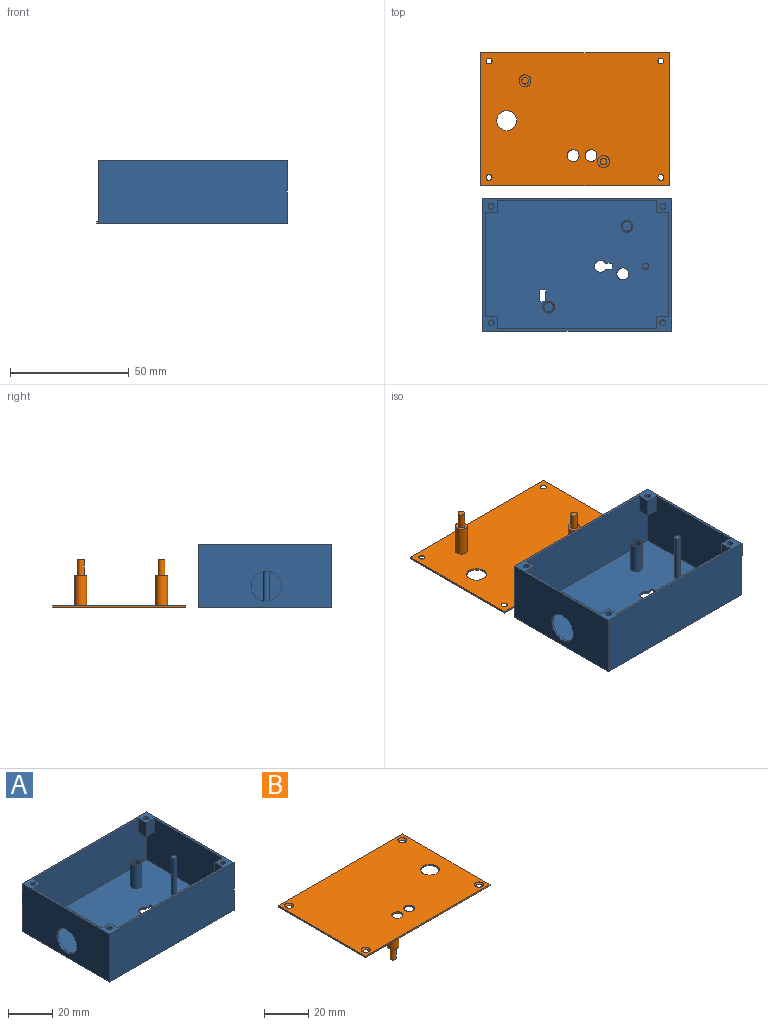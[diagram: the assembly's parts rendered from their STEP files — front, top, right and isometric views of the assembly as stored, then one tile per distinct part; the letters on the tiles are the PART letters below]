
ASSEMBLY  parts=2 mates=1
PART A: 47 faces, bbox 79.4x56x26.4 mm
  f0: plane 79.38x56.05mm, normal (0,0,-1), area 4390.6mm2, adj f6,f7,f8,f9,f10,f36,f37,f38
  f1: plane 77.38x54.05mm, normal (0,0,1), area 4079.4mm2, adj f2,f3,f4,f5,f10,f12,f16,f36
  f2: plane 54.05x25.4mm, normal (-1,0,0), area 1295.3mm2, adj f1,f3,f5,f19,f24,f27,f33,f35
  f3: plane 77.38x25.4mm, normal (0,1,0), area 1888.1mm2, adj f1,f2,f4,f19,f26,f27,f28,f31
  f4: plane 54.05x25.4mm, normal (1,0,0), area 1168.7mm2, adj f1,f3,f5,f19,f22,f23,f30,f31
  f5: plane 77.38x25.4mm, normal (0,-1,0), area 1888.1mm2, adj f1,f2,f4,f19,f20,f23,f32,f35
  f6: plane 56.05x26.4mm, normal (-1,0,0), area 1352.9mm2, adj f0,f7,f9,f19,f40
  f7: plane 79.38x26.4mm, normal (0,-1,0), area 2095.7mm2, adj f0,f6,f8,f19
  f8: plane 56.05x26.4mm, normal (1,0,0), area 1479.6mm2, adj f0,f7,f9,f19
  f9: plane 79.38x26.4mm, normal (0,1,0), area 2095.7mm2, adj f0,f6,f8,f19
  f10: cylinder r=2.5mm len=5mm, axis (0,0,1), area 15.7mm2, adj f0,f1
  f11: cylinder r=2mm len=12.7mm, axis (0,0,-1), area 159.5mm2, adj f13,f14
  f12: cylinder r=2.5mm len=12.7mm, axis (0,0,-1), area 199.4mm2, adj f1,f13
  f13: plane 5x5mm, normal (0,0,1), area 7.1mm2, adj f11,f12
  f14: plane 4x4mm, normal (0,0,1), area 12.5mm2, adj f11
  f15: cylinder r=2mm len=12.7mm, axis (0,0,-1), area 159.5mm2, adj f17,f18
  f16: cylinder r=2.5mm len=12.7mm, axis (0,0,-1), area 199.4mm2, adj f1,f17
  f17: plane 5x5mm, normal (0,0,1), area 7.1mm2, adj f15,f16
  f18: plane 4x4mm, normal (0,0,1), area 12.5mm2, adj f15
  f19: plane 79.38x56.05mm, normal (0,0,1), area 350.4mm2, adj f2,f3,f4,f5,f6,f7,f8,f9
  f20: plane 7.62x5.08mm, normal (1,0,0), area 38.7mm2, adj f5,f19,f22,f23
  f21: cylinder r=1.25mm len=7.62mm, axis (0,0,-1), area 59.8mm2, adj f19,f23
  f22: plane 7.62x5.08mm, normal (0,-1,0), area 38.7mm2, adj f4,f19,f20,f23
  f23: plane 5.08x5.08mm, normal (0,0,-1), area 20.9mm2, adj f4,f5,f20,f21,f22
  f24: plane 7.62x5.08mm, normal (0,1,0), area 38.7mm2, adj f2,f19,f26,f27
  f25: cylinder r=1.25mm len=7.62mm, axis (0,0,-1), area 59.8mm2, adj f19,f27
  f26: plane 7.62x5.08mm, normal (-1,0,0), area 38.7mm2, adj f3,f19,f24,f27
  f27: plane 5.08x5.08mm, normal (0,0,-1), area 20.9mm2, adj f2,f3,f24,f25,f26
  f28: plane 7.62x5.08mm, normal (1,0,0), area 38.7mm2, adj f3,f19,f30,f31
  f29: cylinder r=1.25mm len=7.62mm, axis (0,0,-1), area 59.8mm2, adj f19,f31
  f30: plane 7.62x5.08mm, normal (0,1,0), area 38.7mm2, adj f4,f19,f28,f31
  f31: plane 5.08x5.08mm, normal (0,0,-1), area 20.9mm2, adj f3,f4,f28,f29,f30
  f32: plane 7.62x5.08mm, normal (-1,0,0), area 38.7mm2, adj f5,f19,f33,f35
  f33: plane 7.62x5.08mm, normal (0,-1,0), area 38.7mm2, adj f2,f19,f32,f35
  f34: cylinder r=1.25mm len=7.62mm, axis (0,0,-1), area 59.8mm2, adj f19,f35
  f35: plane 5.08x5.08mm, normal (0,0,-1), area 20.9mm2, adj f2,f5,f32,f33,f34
  f36: cylinder r=2.5mm len=5mm, axis (0,0,-1), area 13.1mm2, adj f0,f1,f37,f39
  f37: plane 2.91x1mm, normal (0,-1,0), area 2.9mm2, adj f0,f1,f36,f38
  f38: plane 2.49x1mm, normal (-1,0,0), area 2.5mm2, adj f0,f1,f37,f39
  f39: plane 2.91x1mm, normal (0,1,0), area 2.9mm2, adj f0,f1,f36,f38
  f40: cylinder r=6.35mm len=12.7mm, axis (-1,0,0), area 39.9mm2, adj f4,f6
  f41: cylinder r=1.27mm len=20.32mm, axis (0,0,-1), area 162.1mm2, adj f1,f42
  f42: plane 2.54x2.54mm, normal (0,0,1), area 5.1mm2, adj f41
  f43: plane 2.5x1mm, normal (0,-1,0), area 2.5mm2, adj f0,f1,f44,f46
  f44: plane 5x1mm, normal (1,0,0), area 5mm2, adj f0,f1,f43,f45
  f45: plane 2.5x1mm, normal (0,1,0), area 2.5mm2, adj f0,f1,f44,f46
  f46: plane 5x1mm, normal (-1,0,0), area 5mm2, adj f0,f1,f43,f45
PART B: 25 faces, bbox 79.4x56x20.1 mm
  f0: cylinder r=1.4mm len=6.6mm, axis (0,0,-1), area 58mm2, adj f1,f3
  f1: plane 2.8x2.8mm, normal (0,0,-1), area 6.1mm2, adj f0
  f2: cylinder r=2.5mm len=12.7mm, axis (0,0,-1), area 199.4mm2, adj f3,f17
  f3: plane 5x5mm, normal (0,0,-1), area 13.5mm2, adj f0,f2
  f4: cylinder r=1.4mm len=6.6mm, axis (0,0,-1), area 58mm2, adj f5,f7
  f5: plane 2.8x2.8mm, normal (0,0,-1), area 6.1mm2, adj f4
  f6: cylinder r=2.5mm len=12.7mm, axis (0,0,-1), area 199.4mm2, adj f7,f17
  f7: plane 5x5mm, normal (0,0,-1), area 13.5mm2, adj f4,f6
  f8: plane 56.05x0.76mm, normal (-1,0,0), area 42.7mm2, adj f9,f14,f16,f17
  f9: plane 79.38x0.76mm, normal (0,-1,0), area 60.5mm2, adj f8,f10,f16,f17
  f10: plane 56.05x0.76mm, normal (1,0,0), area 42.7mm2, adj f9,f14,f16,f17
  f11: cylinder r=1.25mm len=2.5mm, axis (0,0,-1), area 0.1mm2, adj f17,f21
  f12: cylinder r=1.25mm len=2.5mm, axis (0,0,-1), area 0.1mm2, adj f17,f22
  f13: cylinder r=1.25mm len=2.5mm, axis (0,0,-1), area 0.1mm2, adj f17,f20
  f14: plane 79.38x0.76mm, normal (0,1,0), area 60.5mm2, adj f8,f10,f16,f17
  f15: cylinder r=1.25mm len=2.5mm, axis (0,0,-1), area 0.1mm2, adj f17,f23
  f16: plane 79.38x56.05mm, normal (0,0,1), area 4304.3mm2, adj f8,f9,f10,f14,f18,f19,f20,f21
  f17: plane 79.38x56.05mm, normal (0,0,-1), area 4295.7mm2, adj f2,f6,f8,f9,f10,f11,f12,f13
  f18: cylinder r=2.5mm len=5mm, axis (0,0,-1), area 12mm2, adj f16,f17
  f19: cylinder r=2.5mm len=5mm, axis (0,0,-1), area 12mm2, adj f16,f17
  f20: cone r=1.25mm half-angle=45deg, axis (0,0,1), area 10.8mm2, adj f13,f16
  f21: cone r=1.25mm half-angle=45deg, axis (0,0,1), area 10.8mm2, adj f11,f16
  f22: cone r=1.25mm half-angle=45deg, axis (0,0,1), area 10.8mm2, adj f12,f16
  f23: cone r=1.25mm half-angle=45deg, axis (0,0,1), area 10.8mm2, adj f15,f16
  f24: cylinder r=4.19mm len=8.38mm, axis (0,0,-1), area 20.1mm2, adj f16,f17
PLACE A rot(axis=(0,1,0),0deg) t=(-141.28,-13.33,73.42)mm
PLACE B rot(axis=(0,-1,0),180deg) t=(-145.8,47.91,98.83)mm
MATE planar B.f16 <-> A.f0  axis (0,0,-1) through (-143.64,48.65,72.42)mm
